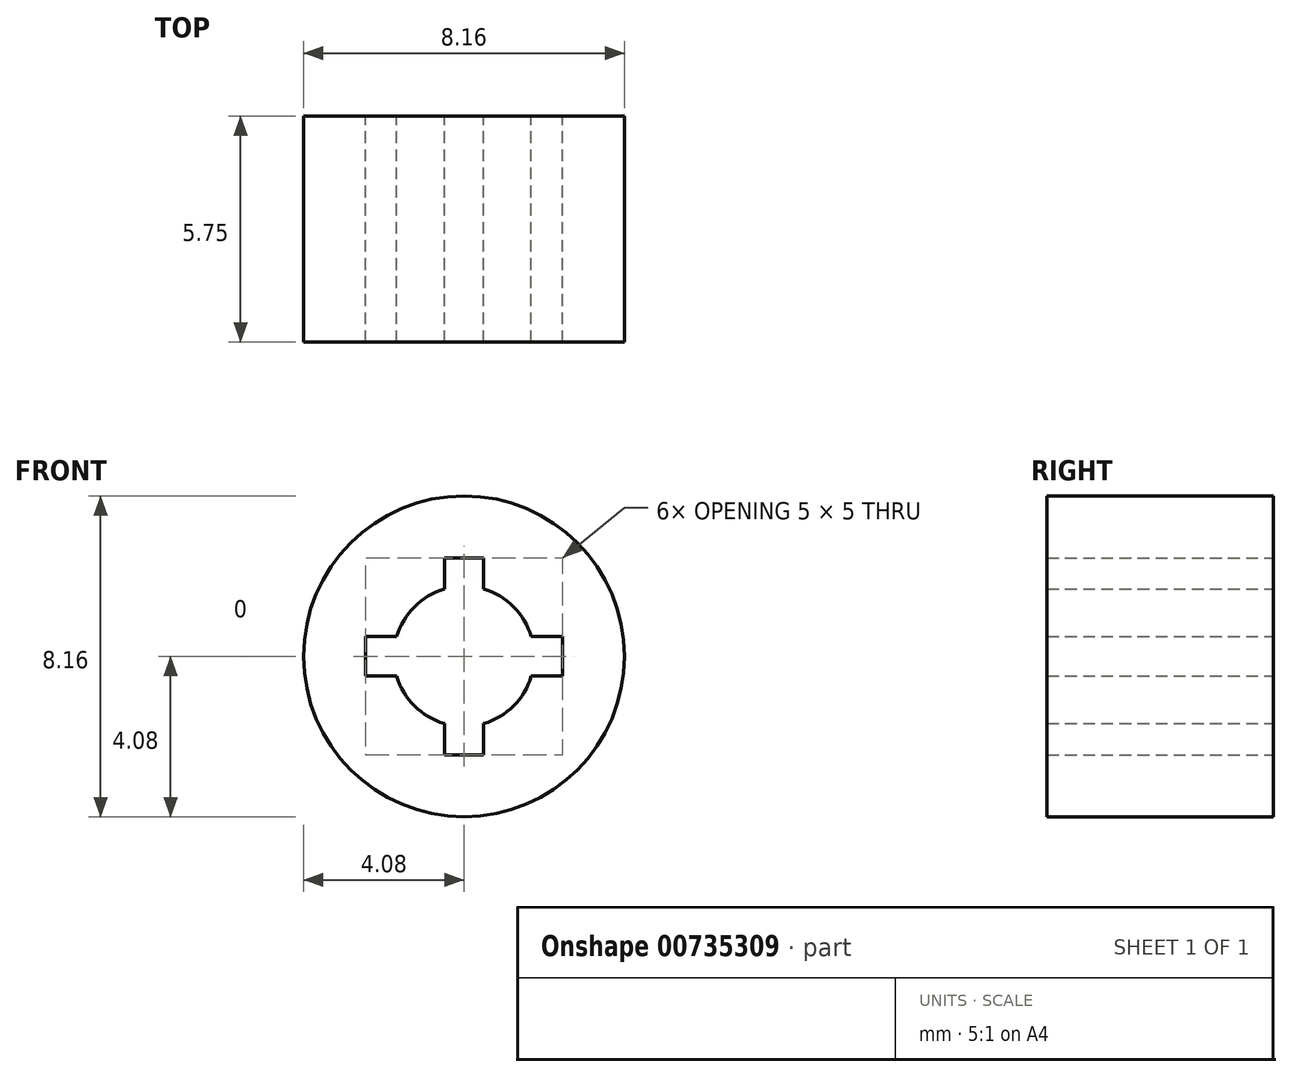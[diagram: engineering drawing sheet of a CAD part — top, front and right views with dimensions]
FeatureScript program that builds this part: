
annotation { "Feature Type Name" : "Feature", "Feature Type Description" : "" }
export const myFeature = defineFeature(function(context is Context, id is Id, definition is map)
    precondition{}
    {
        {
            var Q0;
            Q0=qCreatedBy(makeId("Front.planeOp"),FACE);
            var sketch = newSketch(context, id + "F0", { "sketchPlane" : qUnion([Q0])});
            skCircle(sketch, "E0", {"center": v(0, 0) * mm, "radius": 4.08 * mm});
            skLineSegment(sketch, "E1", {"start": v(0.5, 2.5) * mm, "end": v(-0.5, 2.5) * mm});
            skLineSegment(sketch, "E2", {"start": v(0.5, -2.5) * mm, "end": v(-0.5, -2.5) * mm});
            skLineSegment(sketch, "E3", {"start": v(-2.5, 0.5) * mm, "end": v(-2.5, -0.5) * mm});
            skLineSegment(sketch, "E4", {"start": v(2.5, 0.5) * mm, "end": v(2.5, -0.5) * mm});
            skArc(sketch, "E5", {"start": v(-0.5, 1.7) * mm, "mid": v(-1.26, 1.26) * mm, "end": v(-1.7, 0.5) * mm});
            skLineSegment(sketch, "E6", {"start": v(-0.5, 2.5) * mm, "end": v(-0.5, 1.7) * mm});
            skLineSegment(sketch, "E7", {"start": v(0.5, 2.5) * mm, "end": v(0.5, 1.7) * mm});
            skLineSegment(sketch, "E8", {"start": v(-2.5, 0.5) * mm, "end": v(-1.7, 0.5) * mm});
            skLineSegment(sketch, "E9", {"start": v(-2.5, -0.5) * mm, "end": v(-1.7, -0.5) * mm});
            skLineSegment(sketch, "E10", {"start": v(2.5, 0.5) * mm, "end": v(1.7, 0.5) * mm});
            skLineSegment(sketch, "E11", {"start": v(2.5, -0.5) * mm, "end": v(1.7, -0.5) * mm});
            skLineSegment(sketch, "E12", {"start": v(-0.5, -2.5) * mm, "end": v(-0.5, -1.7) * mm});
            skLineSegment(sketch, "E13", {"start": v(0.5, -2.5) * mm, "end": v(0.5, -1.7) * mm});
            skArc(sketch, "E14.trimOffspring", {"start": v(-1.7, -0.5) * mm, "mid": v(-1.26, -1.26) * mm, "end": v(-0.5, -1.7) * mm});
            skArc(sketch, "E15.trimOffspring", {"start": v(1.7, 0.5) * mm, "mid": v(1.26, 1.26) * mm, "end": v(0.5, 1.7) * mm});
            skArc(sketch, "E16.trimOffspring", {"start": v(0.5, -1.7) * mm, "mid": v(1.26, -1.26) * mm, "end": v(1.7, -0.5) * mm});
            skPoint(sketch, "E17.start.orphan", {"position": v(-4.08, 0) * mm});
            skPoint(sketch, "E18.start.orphan", {"position": v(0, 4.08) * mm});
            skPoint(sketch, "E19.start.orphan", {"position": v(0, -4.08) * mm});
            skPoint(sketch, "E20.start.orphan", {"position": v(4.08, 0) * mm});
            skSolve(sketch);
        }
        {
            var Q0;
            Q0=qSketchRegion(id+"F0",true);
            extrude(context, id + "F1", {"entities" : qUnion([Q0]), "depth" : 5.75 * mm, "offsetDistance" : 25 * mm});
        }
    });
